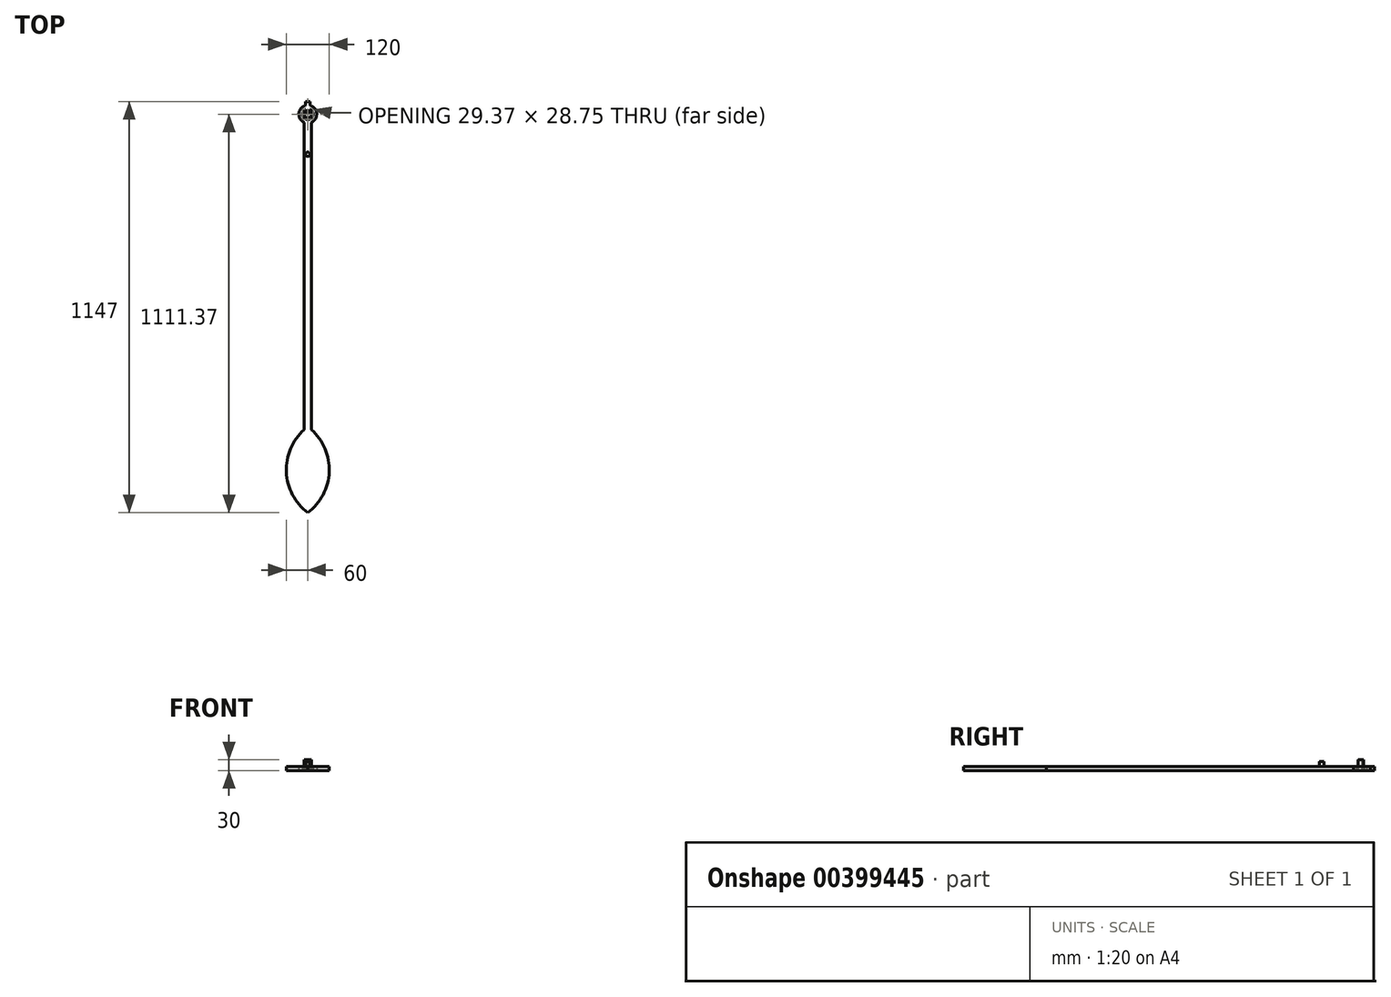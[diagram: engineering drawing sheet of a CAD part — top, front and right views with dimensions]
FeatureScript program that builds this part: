
annotation { "Feature Type Name" : "Feature", "Feature Type Description" : "" }
export const myFeature = defineFeature(function(context is Context, id is Id, definition is map)
    precondition{}
    {
        {
            var Q0;
            Q0=qCreatedBy(makeId("Top.planeOp"),FACE);
            var sketch = newSketch(context, id + "F0", { "sketchPlane" : qUnion([Q0])});
            skArc(sketch, "E0", {"start": v(-6, 13.75) * mm, "mid": v(0, -15) * mm, "end": v(6, 13.75) * mm});
            skArc(sketch, "E1", {"start": v(10, -22.91) * mm, "mid": v(24.91, 2.11) * mm, "end": v(6, 24.27) * mm});
            skLineSegment(sketch, "E2.bottom", {"start": v(-6, 35) * mm, "end": v(6, 35) * mm});
            skLineSegment(sketch, "E2.left", {"start": v(-6, 35) * mm, "end": v(-6, 24.27) * mm});
            skLineSegment(sketch, "E2.right", {"start": v(6, 35) * mm, "end": v(6, 24.27) * mm});
            skLineSegment(sketch, "E3", {"start": v(-6, 7.15) * mm, "end": v(0, 0) * mm});
            skLineSegment(sketch, "E4", {"start": v(6, 7.15) * mm, "end": v(0, 0) * mm});
            skLineSegment(sketch, "E5.left", {"start": v(-10, -22.91) * mm, "end": v(-10, -880.2) * mm});
            skLineSegment(sketch, "E5.right", {"start": v(10, -22.91) * mm, "end": v(10, -880.2) * mm});
            skPoint(sketch, "E5.middle", {"position": v(0, -507.46) * mm});
            skArc(sketch, "E6", {"start": v(-10, -880.2) * mm, "mid": v(-59.86, -998.46) * mm, "end": v(0, -1112) * mm});
            skPoint(sketch, "E6.centerSnap0", {"position": v(0, -992) * mm});
            skArc(sketch, "E7", {"start": v(0, -1112) * mm, "mid": v(59.86, -998.46) * mm, "end": v(10, -880.2) * mm});
            skPoint(sketch, "E8.orphan", {"position": v(-10, -992) * mm});
            skPoint(sketch, "E5.top.end.orphan", {"position": v(10, -992) * mm});
            skArc(sketch, "E9.trimOffspring", {"start": v(-6, 24.27) * mm, "mid": v(-24.91, 2.11) * mm, "end": v(-10, -22.91) * mm});
            skLineSegment(sketch, "E10.trimOffspring", {"start": v(-6, 13.75) * mm, "end": v(-6, 7.15) * mm});
            skLineSegment(sketch, "E11.trimOffspring", {"start": v(6, 13.75) * mm, "end": v(6, 7.15) * mm});
            skSolve(sketch);
        }
        {
            var Q0;
            Q0 = qSketchRegion(id + "F0", true);
            extrude(context, id + "F1", {"entities" : qUnion([Q0]), "depth" : 12 * mm});
        }
        {
            var Q0;
            Q0=qCreatedBy(makeId("Top.planeOp"),FACE);
            var sketch = newSketch(context, id + "F2", { "sketchPlane" : qUnion([Q0])});
            skArc(sketch, "E12", {"start": v(-9.06, 4.23) * mm, "mid": v(0, -10) * mm, "end": v(9.06, 4.23) * mm});
            skLineSegment(sketch, "E13", {"start": v(-9.06, 4.23) * mm, "end": v(0, 0) * mm});
            skLineSegment(sketch, "E14", {"start": v(0, 0) * mm, "end": v(9.06, 4.23) * mm});
            skSolve(sketch);
        }
        {
            var Q0;
            Q0 = qSketchRegion(id + "F2", true);
            extrude(context, id + "F3", {"entities" : qUnion([Q0]), "depth" : 30 * mm});
        }
        {
            var Q0;
            Q0=qCreatedBy(makeId("Top.planeOp"),FACE);
            var sketch = newSketch(context, id + "F4", { "sketchPlane" : qUnion([Q0])});
            skCircle(sketch, "E15", {"center": v(0, -112) * mm, "radius": 6 * mm});
            skSolve(sketch);
        }
        {
            var Q0;
            Q0 = qSketchRegion(id + "F4", true);
            extrude(context, id + "F5", {"entities" : qUnion([Q0]), "operationType" : NewBodyOperationType.ADD, "depth" : 25 * mm});
        }
    });
